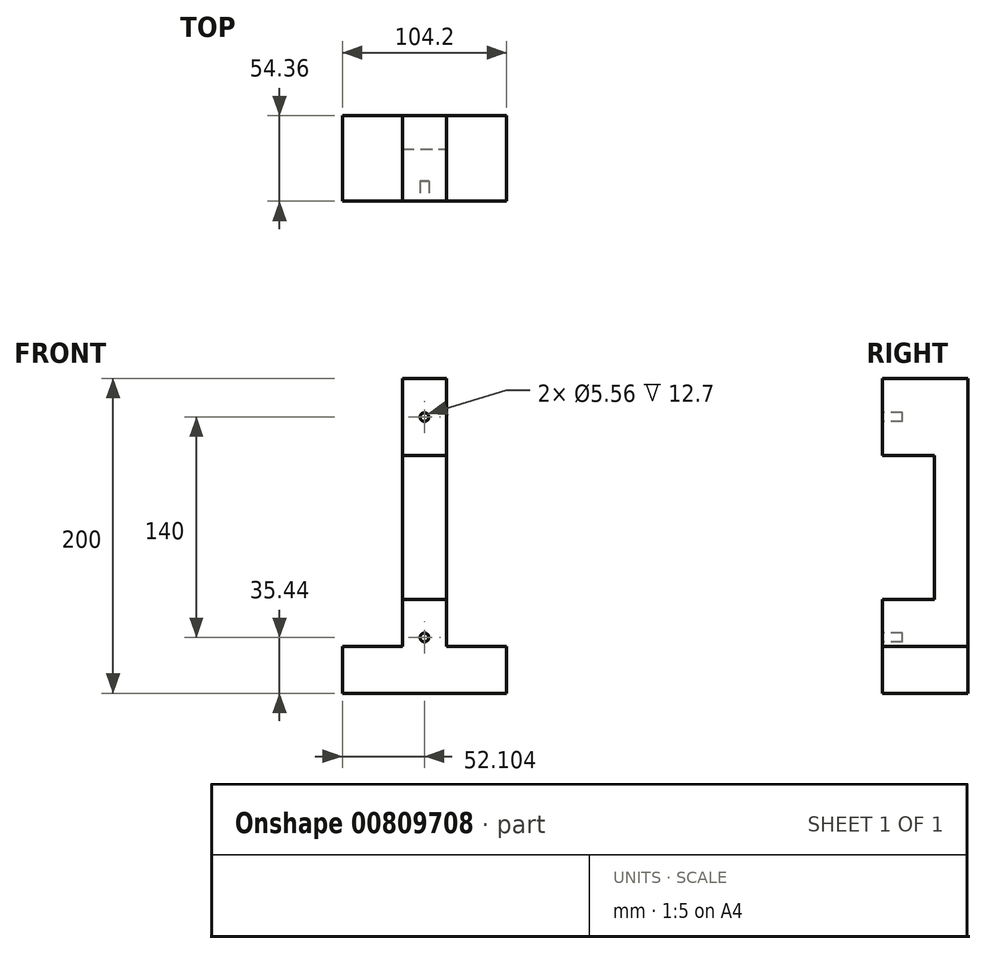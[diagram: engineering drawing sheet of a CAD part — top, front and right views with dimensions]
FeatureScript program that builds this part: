
annotation { "Feature Type Name" : "Feature", "Feature Type Description" : "" }
export const myFeature = defineFeature(function(context is Context, id is Id, definition is map)
    precondition{}
    {
        {
            var Q0;
            Q0=qCreatedBy(makeId("Front.planeOp"),FACE);
            var sketch = newSketch(context, id + "F0", { "sketchPlane" : qUnion([Q0])});
            skLineSegment(sketch, "E0.bottom", {"start": v(-55.94, 169.56) * mm, "end": v(-27.94, 169.56) * mm});
            skLineSegment(sketch, "E0.top", {"start": v(-55.94, -30.44) * mm, "end": v(-27.94, -30.44) * mm});
            skLineSegment(sketch, "E0.left", {"start": v(-55.94, 169.56) * mm, "end": v(-55.94, -30.44) * mm});
            skLineSegment(sketch, "E0.right", {"start": v(-27.94, 169.56) * mm, "end": v(-27.94, -30.44) * mm});
            skSolve(sketch);
        }
        {
            var Q0;
            Q0 = qSketchRegion(id + "F0", true);
            extrude(context, id + "F1", {"entities" : qUnion([Q0]), "depth" : 54.36 * mm, "offsetDistance" : 25.4 * mm});
        }
        {
            var Q0;
            Q0=makeQuery(id+"F1.opExtrude","CAP_FACE",FACE,{"disambiguationData":[OSD([sQuery(id+"F0.wireOp",EDGE,"E0.bottom"),sQuery(id+"F0.wireOp",EDGE,"E0.top"),sQuery(id+"F0.wireOp",EDGE,"E0.left"),sQuery(id+"F0.wireOp",EDGE,"E0.right")])],"isStart":false});
            var sketch = newSketch(context, id + "F2", { "sketchPlane" : qUnion([Q0])});
            skLineSegment(sketch, "E1.bottom", {"start": v(-55.94, 150) * mm, "end": v(-27.94, 150) * mm});
            skLineSegment(sketch, "E1.top", {"start": v(-55.94, 0) * mm, "end": v(-27.94, 0) * mm});
            skLineSegment(sketch, "E1.left", {"start": v(-55.94, 150) * mm, "end": v(-55.94, 0) * mm});
            skLineSegment(sketch, "E1.right", {"start": v(-27.94, 150) * mm, "end": v(-27.94, 0) * mm});
            skSolve(sketch);
        }
        {
            var Q0;
            Q0=makeQuery(id+"F2.imprint","IMPRINT",FACE,{"disambiguationData":[TD([[makeQuery(id+"F2.imprint","IMPRINT",EDGE,{"derivedFrom":sQuery(id+"F2.wireOp",EDGE,"E1.bottom")}),-1.0]])]});
            var sketch = newSketch(context, id + "F3", { "sketchPlane" : qUnion([Q0])});
            skLineSegment(sketch, "E2.bottom", {"start": v(-55.64, 120.73) * mm, "end": v(-27.54, 120.73) * mm});
            skLineSegment(sketch, "E2.top", {"start": v(-55.64, 29.29) * mm, "end": v(-27.54, 29.29) * mm});
            skLineSegment(sketch, "E2.left", {"start": v(-55.64, 120.73) * mm, "end": v(-55.64, 29.29) * mm});
            skLineSegment(sketch, "E2.right", {"start": v(-27.54, 120.73) * mm, "end": v(-27.54, 29.29) * mm});
            skSolve(sketch);
        }
        {
            var Q0;
            {var subQ0=sQuery(id+"F3.wireOp",EDGE,"E2.left");Q0=makeQuery(id+"F3.imprint","IMPRINT",FACE,{"disambiguationData":[TD([[makeQuery(id+"F3.imprint","IMPRINT",EDGE,{"derivedFrom":subQ0}),1.0]])]});}
            extrude(context, id + "F4", {"entities" : qUnion([Q0]), "operationType" : NewBodyOperationType.REMOVE, "oppositeDirection" : true, "depth" : 33 * mm, "offsetDistance" : 25.4 * mm});
        }
        {
            var Q0;
            Q0=makeQuery(id+"F4.boolean.opBoolean","COPY",FACE,{"derivedFrom":makeQuery(id+"F4.opExtrude","SWEPT_FACE",FACE,{"disambiguationData":[OSD([sQuery(id+"F3.wireOp",EDGE,"E2.left")])]})});
            extrude(context, id + "F5", {"entities" : qUnion([Q0]), "operationType" : NewBodyOperationType.REMOVE, "oppositeDirection" : true, "depth" : 25.4 * mm, "offsetDistance" : 25.4 * mm});
        }
        {
            var Q0;
            Q0=makeQuery(id+"F2.imprint","IMPRINT",FACE,{"disambiguationData":[TD([[makeQuery(id+"F2.imprint","IMPRINT",EDGE,{"derivedFrom":sQuery(id+"F2.wireOp",EDGE,"E1.bottom")}),-1.0]])]});
            var sketch = newSketch(context, id + "F6", { "sketchPlane" : qUnion([Q0])});
            skCircle(sketch, "E3", {"center": v(-41.94, 145) * mm, "radius": 2.78 * mm});
            skCircle(sketch, "E4", {"center": v(-41.94, 5) * mm, "radius": 2.78 * mm});
            skSolve(sketch);
        }
        {
            var Q0;
            Q0 = qSketchRegion(id + "F6", true);
            extrude(context, id + "F7", {"entities" : qUnion([Q0]), "operationType" : NewBodyOperationType.REMOVE, "oppositeDirection" : true, "depth" : 12.7 * mm, "offsetDistance" : 25.4 * mm});
        }
        {
            var Q0;
            Q0=makeQuery(id+"F1.opExtrude","SWEPT_FACE",FACE,{"disambiguationData":[OSD([sQuery(id+"F0.wireOp",EDGE,"E0.right")])]});
            var sketch = newSketch(context, id + "F8", { "sketchPlane" : qUnion([Q0])});
            skLineSegment(sketch, "E5.bottom", {"start": v(-54.36, -0.57) * mm, "end": v(0, -0.57) * mm});
            skLineSegment(sketch, "E5.top", {"start": v(-54.36, -30.44) * mm, "end": v(0, -30.44) * mm});
            skLineSegment(sketch, "E5.left", {"start": v(-54.36, -0.57) * mm, "end": v(-54.36, -30.44) * mm});
            skLineSegment(sketch, "E5.right", {"start": v(0, -0.57) * mm, "end": v(0, -30.44) * mm});
            skSolve(sketch);
        }
        {
            var Q0;
            Q0 = qSketchRegion(id + "F8", true);
            extrude(context, id + "F9", {"entities" : qUnion([Q0]), "operationType" : NewBodyOperationType.ADD, "depth" : 38.1 * mm, "offsetDistance" : 25.4 * mm});
        }
        {
            var Q0;
            Q0=makeQuery(id+"F1.opExtrude","SWEPT_FACE",FACE,{"disambiguationData":[OSD([sQuery(id+"F0.wireOp",EDGE,"E0.left")])]});
            var sketch = newSketch(context, id + "F10", { "sketchPlane" : qUnion([Q0])});
            skLineSegment(sketch, "E6.bottom", {"start": v(54.36, -0.57) * mm, "end": v(0, -0.57) * mm});
            skLineSegment(sketch, "E6.top", {"start": v(54.36, -30.44) * mm, "end": v(0, -30.44) * mm});
            skLineSegment(sketch, "E6.left", {"start": v(54.36, -0.57) * mm, "end": v(54.36, -30.44) * mm});
            skLineSegment(sketch, "E6.right", {"start": v(0, -0.57) * mm, "end": v(0, -30.44) * mm});
            skSolve(sketch);
        }
        {
            var Q0;
            Q0 = qSketchRegion(id + "F10", true);
            extrude(context, id + "F11", {"entities" : qUnion([Q0]), "operationType" : NewBodyOperationType.ADD, "depth" : 38.1 * mm, "offsetDistance" : 25.4 * mm});
        }
    });
